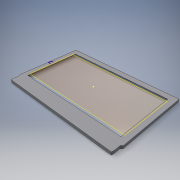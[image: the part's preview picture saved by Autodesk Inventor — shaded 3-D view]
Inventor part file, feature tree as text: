
AUTODESK INVENTOR PART (.ipt)
format: ipt  version: 2017 (Build 210142000, 142)  size: 405,504 bytes
history: native  units: mm
features: extrude x12, sketch x12, projected_geometry x5, other x3, reference x2, plane x1, chamfer x1
ambient origin geometry x8: Origin, YZ Plane, XZ Plane, XY Plane, X Axis, Y Axis, Z Axis, Center Point
bodies: Volumenkörper1 (feature_tree)
feature tree (36):
  plane  "Arbeitsebene1"
  extrude  "Extrusion1"  Depth=1.0mm
  extrude  "Extrusion2"  Depth=1.0mm
  extrude  "Extrusion3"  Depth=1.0mm TaperAngle=0.0deg
  chamfer  "Fase1"  Distance=1.0mm
  extrude  "Extrusion4"  Depth=2.0mm TaperAngle=0.0deg
  extrude  "Extrusion6"  Depth=2.0mm
  extrude  "Extrusion7"  Depth=2.0mm
  extrude  "Extrusion8"  Depth=0.7mm TaperAngle=0.0deg
  extrude  "Extrusion9"  Depth=2.5mm
  extrude  "Extrusion10"  Depth=2.5mm
  extrude  "Extrusion11"  Depth=2.5mm
  extrude  "Extrusion12"  Depth=1.7mm TaperAngle=0.0deg
  extrude  "Extrusion13"  Depth=2.3mm TaperAngle=0.0deg
  sketch  "Skizze1"  dims[d0=1.0mm d1=1.0mm]
  reference  "Referenz1"
  sketch  "Skizze2"  dims[d2=1.0mm d3=1.0mm]
  projected_geometry  "Projizierte Kontur1"
  reference  "Referenz2"
  sketch  "Skizze3"  dims[d4=1.0mm d5=0.0mm d6=1.0mm d7=0.0mm]
  projected_geometry  "Projizierte Kontur2"
  sketch  "Skizze4"  dims[d8=2.0mm]
  projected_geometry  "Projizierte Kontur3"
  sketch  "Skizze9"  dims[d9=2.0mm]
  sketch  "Skizze10"  dims[d10=2.0mm]
  sketch  "Skizze11"  dims[d11=2.0mm d12=1.0mm d13=0.0mm]
  projected_geometry  "Projizierte Kontur8"
  projected_geometry  "Projizierte Kontur9"
  sketch  "Skizze12"  dims[d14=1.0mm d15=2.0mm d16=45.0deg d17=0.7mm d18=0.0mm]
  sketch  "Skizze13"  dims[d21=0.7mm d22=0.0mm d23=2.0mm]
  sketch  "Skizze15"  dims[d24=0.7mm d25=0.0mm d26=2.0mm]
  sketch  "Skizze16"  dims[d27=0.7mm d28=0.0mm d29=0.7mm d30=0.0mm]
  sketch  "Skizze18"  dims[d32=2.5mm d33=2.5mm d34=2.5mm d35=2.5mm d36=1.7mm d37=1.0mm d38=0.0mm d39=0.0mm d40=2.3mm d41=0.0mm d42=10.0mm d43=0.0mm d44=3.05mm d45=3.05mm d46=0.2mm d47=3.05mm d48=3.05mm d49=0.2mm d50=10.0mm d51=0.0mm]
  other  "<userpath>\Dropbox\Elektronik\aXe_Dashboard240XL\Gehäuse\DisplayDummyAuschnitt.iam"
  other  "DisplayDummyAuschnitt.iam"
  other  "DisplayDummy:1"
